# Revit family: Door_Hatch_Watertight_WalzKrenzer_WTH-R-Rect
name_source: partatom
category: Generic Models
units: mm (PartAtom-declared; Revit-internal decimal feet)

## family parameters
Can host rebar = No
Classification Number = 23.30.10.21.37.17
Cut with Voids When Loaded = No
Host = Face
Maintain Annotation Orientation = No
Part Type = Normal
Room Calculation Point = No
Round Connector Dimension = Use Diameter
Shared = No

## types (6) — shared parameters
Assembly Code = E1090900
Default Elevation = 0' - 0"
Keynote = 08392
Manufacturer = Walz & Krenzer, Inc.
Manufacturer Fax = 203-267-5716
Manufacturer Website = http://www.floodbarriers.com
Model = WTH-R
Product Data = http://www.arcat.com
Revision = R1_2015-06
Sales Information = http://www.floodbarriers.com
Specification = http://www.arcat.com
Test Data = http://www.floodbarriers.com
URL = http://www.floodbarriers.com
zero-valued in all types: Expected Lifespan (Years), Maintenance Schedule (Months), Operating Pressure, Warranty Duration (Years)

## per-type parameters (varying)
| type | Description |
| Power Operated Both Sides | Walz and Krenzer Raised Electric Hinged Flood Hatch - WTH-R as Specified |
| Power Operated Bottom | Walz and Krenzer Raised Electric Hinged Flood Hatch - WTH-R as Specified |
| Power Operated Top | Walz and Krenzer Raised Electric Hinged Flood Hatch - WTH-R as Specified |
| Manually Operable Both Sides | Walz and Krenzer Raised Manual Hinged Flood Hatch - WTH-R as Specified |
| Manually Operable Bottom | Walz and Krenzer Raised Manual Hinged Flood Hatch - WTH-R as Specified |
| Manually Operable Top | Walz and Krenzer Raised Manual Hinged Flood Hatch - WTH-R as Specified |

## geometry (parser evidence)
native form markers: Sweep x1
no freeform markers — native parametric forms only
